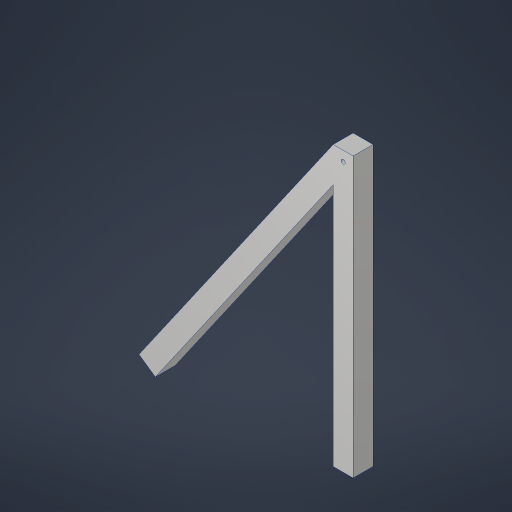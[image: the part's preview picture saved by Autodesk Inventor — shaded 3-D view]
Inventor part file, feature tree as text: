
AUTODESK INVENTOR PART (.ipt)
format: ipt  version: 2023.4 (Build 274418000, 418)  size: 181,248 bytes
history: native  units: in
note: dims shown in document units (in); Inventor stores cm internally (conversion verified against a paired STEP export)
features: sketch x2, extrude x1, hole x1, projected_geometry x1
ambient origin geometry x8: Origin, YZ Plane, XZ Plane, XY Plane, X Axis, Y Axis, Z Axis, Center Point
bodies: Solid1 (feature_tree)
feature tree (5):
  extrude  "Extrusion1"  Depth=14.0in
  hole  "Hole1"  [1 undecoded]
  sketch  "Sketch1"  dims[d0=1.0in d1=14.0in]
  sketch  "Sketch2"  dims[d2=1.0in d3=10.75in d4=1.0in d5=0.0in d6=0.5in d7=0.5in d8=0.201in d9=0.75in d10=0.385in d11=0.25in d12=0.5635in d13=1.0in d14=0.8108in]
  projected_geometry  "Project Cut Edges1"
note: 1 required parameter value undecoded (feature->parameter linkage not recoverable at this tier; creation-order binding heuristic only, values carry confidence <= 0.55)
